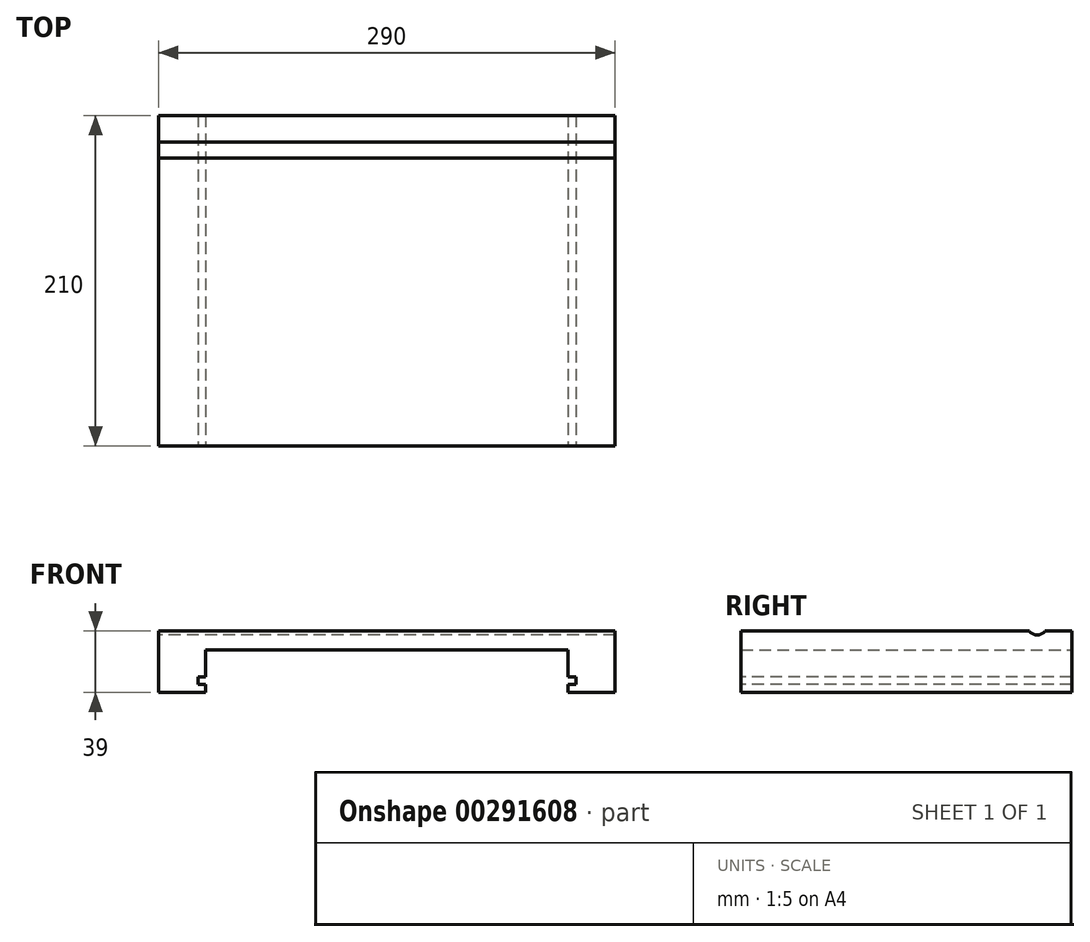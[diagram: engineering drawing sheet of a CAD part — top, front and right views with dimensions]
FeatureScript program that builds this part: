
annotation { "Feature Type Name" : "Feature", "Feature Type Description" : "" }
export const myFeature = defineFeature(function(context is Context, id is Id, definition is map)
    precondition{}
    {
        {
            var Q0;
            Q0=qCreatedBy(makeId("Top.planeOp"),FACE);
            var sketch = newSketch(context, id + "F0", { "sketchPlane" : qUnion([Q0])});
            skLineSegment(sketch, "E0.bottom", {"start": v(145, 105) * mm, "end": v(-145, 105) * mm});
            skLineSegment(sketch, "E0.top", {"start": v(145, -105) * mm, "end": v(-145, -105) * mm});
            skLineSegment(sketch, "E0.left", {"start": v(145, 105) * mm, "end": v(145, -105) * mm});
            skLineSegment(sketch, "E0.right", {"start": v(-145, 105) * mm, "end": v(-145, -105) * mm});
            skPoint(sketch, "E0.middle", {"position": v(0, 0) * mm});
            skSolve(sketch);
        }
        {
            var Q0;
            Q0 = qSketchRegion(id + "F0", true);
            extrude(context, id + "F1", {"entities" : qUnion([Q0]), "oppositeDirection" : true, "depth" : 12 * mm});
        }
        {
            var Q0;
            Q0=makeQuery(id+"F1.opExtrude","CAP_FACE",FACE,{"disambiguationData":[OSD([sQuery(id+"F0.wireOp",EDGE,"E0.bottom"),sQuery(id+"F0.wireOp",EDGE,"E0.top"),sQuery(id+"F0.wireOp",EDGE,"E0.left"),sQuery(id+"F0.wireOp",EDGE,"E0.right")])],"isStart":false});
            var sketch = newSketch(context, id + "F2", { "sketchPlane" : qUnion([Q0])});
            skLineSegment(sketch, "E1.bottom", {"start": v(145, 105) * mm, "end": v(115, 105) * mm});
            skLineSegment(sketch, "E1.top", {"start": v(145, -105) * mm, "end": v(115, -105) * mm});
            skLineSegment(sketch, "E1.left", {"start": v(145, 105) * mm, "end": v(145, -105) * mm});
            skLineSegment(sketch, "E1.right", {"start": v(115, 105) * mm, "end": v(115, -105) * mm});
            skLineSegment(sketch, "E2.bottom", {"start": v(-145, 105) * mm, "end": v(-115, 105) * mm});
            skLineSegment(sketch, "E2.top", {"start": v(-145, -105) * mm, "end": v(-115, -105) * mm});
            skLineSegment(sketch, "E2.left", {"start": v(-145, 105) * mm, "end": v(-145, -105) * mm});
            skLineSegment(sketch, "E2.right", {"start": v(-115, 105) * mm, "end": v(-115, -105) * mm});
            skSolve(sketch);
        }
        {
            var Q0;
            Q0 = qSketchRegion(id + "F2", true);
            extrude(context, id + "F3", {"entities" : qUnion([Q0]), "operationType" : NewBodyOperationType.ADD, "depth" : 27 * mm});
        }
        {
            var Q0;
            Q0=makeQuery(id+"F3.boolean.opBoolean","MERGE",FACE,{"derivedFrom":[makeQuery(id+"F1.opExtrude","SWEPT_FACE",FACE,{"disambiguationData":[OSD([sQuery(id+"F0.wireOp",EDGE,"E0.top")])]}),makeQuery(id+"F3.opExtrude","SWEPT_FACE",FACE,{"disambiguationData":[OSD([sQuery(id+"F2.wireOp",EDGE,"E1.bottom")])]}),makeQuery(id+"F3.opExtrude","SWEPT_FACE",FACE,{"disambiguationData":[OSD([sQuery(id+"F2.wireOp",EDGE,"E2.bottom")])]})]});
            var sketch = newSketch(context, id + "F4", { "sketchPlane" : qUnion([Q0])});
            skLineSegment(sketch, "E3.bottom", {"start": v(-115, -34) * mm, "end": v(-120, -34) * mm});
            skLineSegment(sketch, "E3.top", {"start": v(-115, -29) * mm, "end": v(-120, -29) * mm});
            skLineSegment(sketch, "E3.left", {"start": v(-115, -34) * mm, "end": v(-115, -29) * mm});
            skLineSegment(sketch, "E3.right", {"start": v(-120, -34) * mm, "end": v(-120, -29) * mm});
            skLineSegment(sketch, "E4.bottom", {"start": v(115, -34) * mm, "end": v(120, -34) * mm});
            skLineSegment(sketch, "E4.top", {"start": v(115, -29) * mm, "end": v(120, -29) * mm});
            skLineSegment(sketch, "E4.left", {"start": v(115, -34) * mm, "end": v(115, -29) * mm});
            skLineSegment(sketch, "E4.right", {"start": v(120, -34) * mm, "end": v(120, -29) * mm});
            skSolve(sketch);
        }
        {
            var Q0;
            Q0 = qSketchRegion(id + "F4", true);
            extrude(context, id + "F5", {"entities" : qUnion([Q0]), "operationType" : NewBodyOperationType.REMOVE, "endBound" : BoundingType.THROUGH_ALL, "oppositeDirection" : true, "depth" : 25 * mm});
        }
        {
            var Q0;
            Q0=makeQuery(id+"F3.boolean.opBoolean","MERGE",FACE,{"derivedFrom":[makeQuery(id+"F1.opExtrude","SWEPT_FACE",FACE,{"disambiguationData":[OSD([sQuery(id+"F0.wireOp",EDGE,"E0.right")])]}),makeQuery(id+"F3.opExtrude","SWEPT_FACE",FACE,{"disambiguationData":[OSD([sQuery(id+"F2.wireOp",EDGE,"E2.left")])]})]});
            var sketch = newSketch(context, id + "F6", { "sketchPlane" : qUnion([Q0])});
            skArc(sketch, "E5", {"start": v(-88, 0) * mm, "mid": v(-83, -2.5) * mm, "end": v(-78, 0) * mm});
            skLineSegment(sketch, "E6", {"start": v(-105, -2.5) * mm, "end": v(105, -2.5) * mm});
            skSolve(sketch);
        }
        {
            var Q0;
            {var subQ0=sQuery(id+"F6.wireOp",EDGE,"E5");var subQ1=makeQuery(id+"F1.opExtrude","CAP_EDGE",EDGE,{"disambiguationData":[OSD([sQuery(id+"F0.wireOp",EDGE,"E0.right")])],"isStart":true});var subQ2=makeQuery(id+"F6.imprint","INTERSECT",VERTEX,{"disambiguationData":[OD(0.0)],"derivedFrom":[subQ1,subQ0]});Q0=makeQuery(id+"F6.imprint","IMPRINT",FACE,{"disambiguationData":[TD([[makeQuery(id+"F6.imprint","IMPRINT",EDGE,{"disambiguationData":[TD([[subQ2,-1.0]])],"derivedFrom":subQ0}),1.0]])]});}
            extrude(context, id + "F7", {"entities" : qUnion([Q0]), "operationType" : NewBodyOperationType.REMOVE, "endBound" : BoundingType.THROUGH_ALL, "oppositeDirection" : true, "depth" : 25 * mm});
        }
    });
